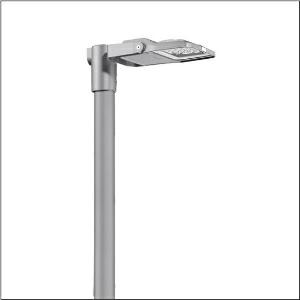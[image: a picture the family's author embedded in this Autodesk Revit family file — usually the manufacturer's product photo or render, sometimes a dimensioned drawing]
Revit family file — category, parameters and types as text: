
# Revit family: floodlight_fl_21_iq_micro___pl64_5xa7762a2e3a_859a
name_source: partatom
category: Lighting Fixtures
units: mm (PartAtom-declared; Revit-internal decimal feet)

## family parameters
Cut with Voids When Loaded = No
Host = Face
Light Source = No
Part Type = Normal
Room Calculation Point = No
Round Connector Dimension = Use Diameter
Shared = No

## types (1)
- --- (1 x LED, 2870 lm, 23.1 W, 3000K)
    Apparent Load = 23 VA
    CIE Flux Codes = 28 80 98 100 100
    Color Rendering = 70
    Color Temperature = 3000K
    Default Elevation = 1800 mm
    Description = Floodlight FL 21 iQ micro, floodlight, primary light control with lens, of PMMA, primary optical cover: protective disc, of toughened safety glass, transparent, light distribution: PL64, light emission: direct distribution, installation type: surface-mounted, LED, High Power LED, rated luminous flux: 2.870lm, luminous efficacy: 124lm/W, light colour: 730, colour temperature: 3000K, control: Auto-Match, Temp-Guard, Night-Set, Smart-Wire, Desk-Remote (wireless, voltage-free reading and setting of iQ features in the workshop via application-optimized NFC function/RFID function), optimised constant luminous flux control (CLO 2.0), Street-Remote, with terminal, 6-pole, mains connection: 220..240V, AC, 50/60Hz, start of lifetime: 23W, end of service life: 24W, reduction: 11W, luminaire housing, of diecast aluminium, powder-coated, Siteco® metallic grey (DB 702S), corrosivity category C5 mid according to DIN EN ISO 12944, sealing non-destructively replaceable, please order mast flange separately, mast bracket, of steel, galvanised, powder-coated, Siteco® metallic grey (DB 702S), protection rating (complete): IP66, insulation class (complete): insulation class II (safety insulation), certification: CE, ENEC, VDE, protection symbol: D, impact resistance: IK07, permissible operating ambient temperature: -40..+40°C, permissible operating ambient temperature for outdoor applications: -40..+50°C, standard: DIN EN 12944, LABS conformity tested according to VDMA 24364:2018-05, packaging unit: 1 piece

Light Distribution: PL64
    Height = 65 mm
    Lamp = 1 x LED
    Lamp Light Flux = 2870 lm
    Lamp Power = 23.1 W
    Lamp count = 1
    Length = 312 mm
    Luminous efficacy = 124 lm/W
    Manufacturer = Siteco
    ModVariant = No
    Model = 5XA7762A2E3A
    Number of Poles = 1
    OnlyDefault = Yes
    Power Factor = 1
    Product Name = Floodlight FL 21 iQ micro | PL64
    Product group = floodlight | pylon annexe
    ProductGroupID = 6200
    Protection Class = Protection class II
    Protection Degree = IP 66
    RLX_Detail_Level = 1
    RLX_Emergency_Light_Flux = 0 lm
    RLX_Emergency_Type = 0
    RLX_Emergency_Type_DB = No
    RlxData = <blob elided: 101653 chars, md5=2ea87228>
    Socket = socket
    Standby Power = 0 W
    System Light Flux = 2870 lm
    System Power = 23 W
    Type Comments = factory setting: luminous flux: 100 % | dim-lin: 254 | 455 mA
    Type Image = l_1007121.jpg
    URL = http://relux.com
    VarID = @adj_152115
    Voltage = 0 V
    Weight = 0.00 kg
    Width = 230 mm

## geometry (parser evidence)
native form markers: Blend x4, Sweep x13
no freeform markers — native parametric forms only
